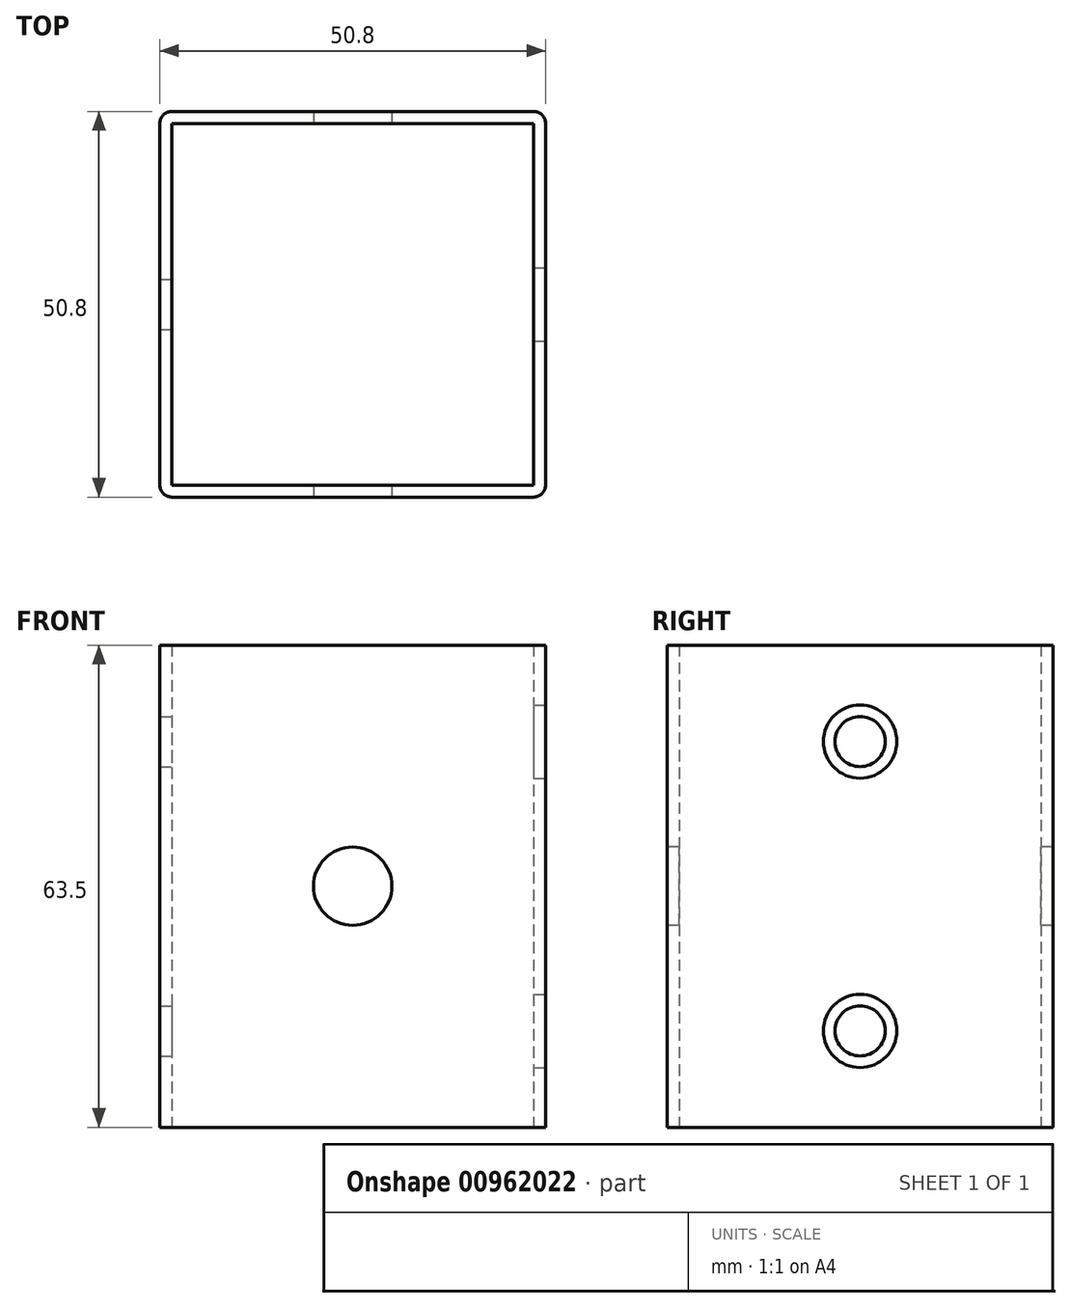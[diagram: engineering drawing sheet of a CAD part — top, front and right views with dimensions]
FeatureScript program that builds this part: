
annotation { "Feature Type Name" : "Feature", "Feature Type Description" : "" }
export const myFeature = defineFeature(function(context is Context, id is Id, definition is map)
    precondition{}
    {
        {
            var Q0;
            Q0=qCreatedBy(makeId("Top.planeOp"),FACE);
            var sketch = newSketch(context, id + "F0", { "sketchPlane" : qUnion([Q0])});
            skLineSegment(sketch, "E0.bottom", {"start": v(25.4, -25.4) * mm, "end": v(-25.4, -25.4) * mm});
            skLineSegment(sketch, "E0.top", {"start": v(25.4, 25.4) * mm, "end": v(-25.4, 25.4) * mm});
            skLineSegment(sketch, "E0.left", {"start": v(25.4, -25.4) * mm, "end": v(25.4, 25.4) * mm});
            skLineSegment(sketch, "E0.right", {"start": v(-25.4, -25.4) * mm, "end": v(-25.4, 25.4) * mm});
            skPoint(sketch, "E0.middle", {"position": v(0, 0) * mm});
            skLineSegment(sketch, "E1.0", {"start": v(23.81, 23.81) * mm, "end": v(-23.81, 23.81) * mm});
            skLineSegment(sketch, "E2.0", {"start": v(-23.81, -23.81) * mm, "end": v(-23.81, 23.81) * mm});
            skLineSegment(sketch, "E3.0", {"start": v(23.81, -23.81) * mm, "end": v(-23.81, -23.81) * mm});
            skLineSegment(sketch, "E4.0", {"start": v(23.81, -23.81) * mm, "end": v(23.81, 23.81) * mm});
            skSolve(sketch);
        }
        {
            var Q0;
            Q0=makeQuery(id+"F0.imprint","IMPRINT",FACE,{"disambiguationData":[TD([[makeQuery(id+"F0.imprint","IMPRINT",EDGE,{"derivedFrom":sQuery(id+"F0.wireOp",EDGE,"E0.bottom")}),-1.0]])]});
            extrude(context, id + "F1", {"entities" : qUnion([Q0]), "depth" : 63.5 * mm, "offsetDistance" : 25.4 * mm});
        }
        {
            var Q0;
            Q0=makeQuery(id+"F1.opExtrude","SWEPT_EDGE",EDGE,{"disambiguationData":[OSD([sQuery(id+"F0.wireOp",EDGE,"E0.bottom"),sQuery(id+"F0.wireOp",EDGE,"E0.left")])]});
            var Q1;
            Q1=makeQuery(id+"F1.opExtrude","SWEPT_EDGE",EDGE,{"disambiguationData":[OSD([sQuery(id+"F0.wireOp",EDGE,"E0.top"),sQuery(id+"F0.wireOp",EDGE,"E0.left")])]});
            var Q2;
            Q2=makeQuery(id+"F1.opExtrude","SWEPT_EDGE",EDGE,{"disambiguationData":[OSD([sQuery(id+"F0.wireOp",EDGE,"E0.bottom"),sQuery(id+"F0.wireOp",EDGE,"E0.right")])]});
            var Q3;
            Q3=makeQuery(id+"F1.opExtrude","SWEPT_EDGE",EDGE,{"disambiguationData":[OSD([sQuery(id+"F0.wireOp",EDGE,"E0.top"),sQuery(id+"F0.wireOp",EDGE,"E0.right")])]});
            fillet(context, id + "F2", {"entities" : qUnion([Q0, Q1, Q2, Q3]), "radius" : 1.59 * mm, "tangentPropagation" : true, "allowEdgeOverflow" : false});
        }
        {
            var Q0;
            Q0=makeQuery(id+"F1.opExtrude","SWEPT_FACE",FACE,{"disambiguationData":[OSD([sQuery(id+"F0.wireOp",EDGE,"E0.left")])]});
            var sketch = newSketch(context, id + "F3", { "sketchPlane" : qUnion([Q0])});
            skCircle(sketch, "E5", {"center": v(0, 50.8) * mm, "radius": 3.3 * mm});
            skCircle(sketch, "E6", {"center": v(0, 12.7) * mm, "radius": 3.3 * mm});
            skSolve(sketch);
        }
        {
            var Q0;
            Q0=sQuery(id+"F3.wireOp",VERTEX,"E6.center");
            var Q1;
            Q1=sQuery(id+"F3.wireOp",VERTEX,"E5.center");
            var Q2;
            Q2=makeQuery(id+"F1.opExtrude","SWEPT_BODY",BODY,{"disambiguationData":[OSD([sQuery(id+"F0.wireOp",EDGE,"E0.bottom"),sQuery(id+"F0.wireOp",EDGE,"E0.top"),sQuery(id+"F0.wireOp",EDGE,"E0.left"),sQuery(id+"F0.wireOp",EDGE,"E0.right"),sQuery(id+"F0.wireOp",EDGE,"E1.0"),sQuery(id+"F0.wireOp",EDGE,"E2.0"),sQuery(id+"F0.wireOp",EDGE,"E3.0"),sQuery(id+"F0.wireOp",EDGE,"E4.0")])]});
            hole(context, id + "F4", {"style" : HoleStyle.SIMPLE, "endStyle" : HoleEndStyle.THROUGH, "holeDiameter" : 6.6 * mm, "majorDiameter" : 6.35 * mm, "isTappedThrough" : true, "tappedDepth" : 12.7 * mm, "tapClearance" : 3, "locations" : qUnion([Q0, Q1]), "scope" : qUnion([Q2])});
        }
        {
            var Q0;
            Q0=makeQuery(id+"F1.opExtrude","SWEPT_FACE",FACE,{"disambiguationData":[OSD([sQuery(id+"F0.wireOp",EDGE,"E0.left")])]});
            var sketch = newSketch(context, id + "F5", { "sketchPlane" : qUnion([Q0])});
            skCircle(sketch, "E7", {"center": v(0, 50.8) * mm, "radius": 4.83 * mm});
            skCircle(sketch, "E8", {"center": v(0, 12.7) * mm, "radius": 4.83 * mm});
            skSolve(sketch);
        }
        {
            var Q0;
            Q0=sQuery(id+"F5.wireOp",VERTEX,"E7.center");
            var Q1;
            Q1=sQuery(id+"F5.wireOp",VERTEX,"E8.center");
            var Q2;
            Q2=makeQuery(id+"F1.opExtrude","SWEPT_BODY",BODY,{"disambiguationData":[OSD([sQuery(id+"F0.wireOp",EDGE,"E0.bottom"),sQuery(id+"F0.wireOp",EDGE,"E0.top"),sQuery(id+"F0.wireOp",EDGE,"E0.left"),sQuery(id+"F0.wireOp",EDGE,"E0.right"),sQuery(id+"F0.wireOp",EDGE,"E1.0"),sQuery(id+"F0.wireOp",EDGE,"E2.0"),sQuery(id+"F0.wireOp",EDGE,"E3.0"),sQuery(id+"F0.wireOp",EDGE,"E4.0")])]});
            hole(context, id + "F6", {"style" : HoleStyle.SIMPLE, "endStyle" : HoleEndStyle.BLIND, "holeDiameter" : 9.65 * mm, "majorDiameter" : 6.35 * mm, "holeDepth" : 12.7 * mm, "isTappedThrough" : true, "tappedDepth" : 12.7 * mm, "tapClearance" : 3, "locations" : qUnion([Q0, Q1]), "scope" : qUnion([Q2])});
        }
        {
            var Q0;
            Q0=makeQuery(id+"F1.opExtrude","SWEPT_FACE",FACE,{"disambiguationData":[OSD([sQuery(id+"F0.wireOp",EDGE,"E0.bottom")])]});
            var sketch = newSketch(context, id + "F7", { "sketchPlane" : qUnion([Q0])});
            skPoint(sketch, "E9", {"position": v(0, 31.75) * mm});
            skSolve(sketch);
        }
        {
            var Q0;
            Q0=sQuery(id+"F7.wireOp",VERTEX,"E9");
            var Q1;
            Q1=makeQuery(id+"F1.opExtrude","SWEPT_BODY",BODY,{"disambiguationData":[OSD([sQuery(id+"F0.wireOp",EDGE,"E0.bottom"),sQuery(id+"F0.wireOp",EDGE,"E0.top"),sQuery(id+"F0.wireOp",EDGE,"E0.left"),sQuery(id+"F0.wireOp",EDGE,"E0.right"),sQuery(id+"F0.wireOp",EDGE,"E1.0"),sQuery(id+"F0.wireOp",EDGE,"E2.0"),sQuery(id+"F0.wireOp",EDGE,"E3.0"),sQuery(id+"F0.wireOp",EDGE,"E4.0")])]});
            hole(context, id + "F8", {"style" : HoleStyle.SIMPLE, "endStyle" : HoleEndStyle.THROUGH, "standardTappedOrClearance" : lookupTablePath({ "standard" : "ANSI", "fit" : "Normal (ASME)", "size" : "3/8", "type" : "Clearance" }), "standardBlindInLast" : lookupTablePath({ "fit" : "Normal", "standard" : "ANSI", "engagement" : "75%", "pitch" : "16 tpi", "size" : "3/8", "type" : "Clearance & tapped" }), "holeDiameter" : 10.3 * mm, "majorDiameter" : 6.35 * mm, "isTappedThrough" : true, "tappedDepth" : 12.7 * mm, "tapClearance" : 3, "locations" : qUnion([Q0]), "scope" : qUnion([Q1])});
        }
    });
